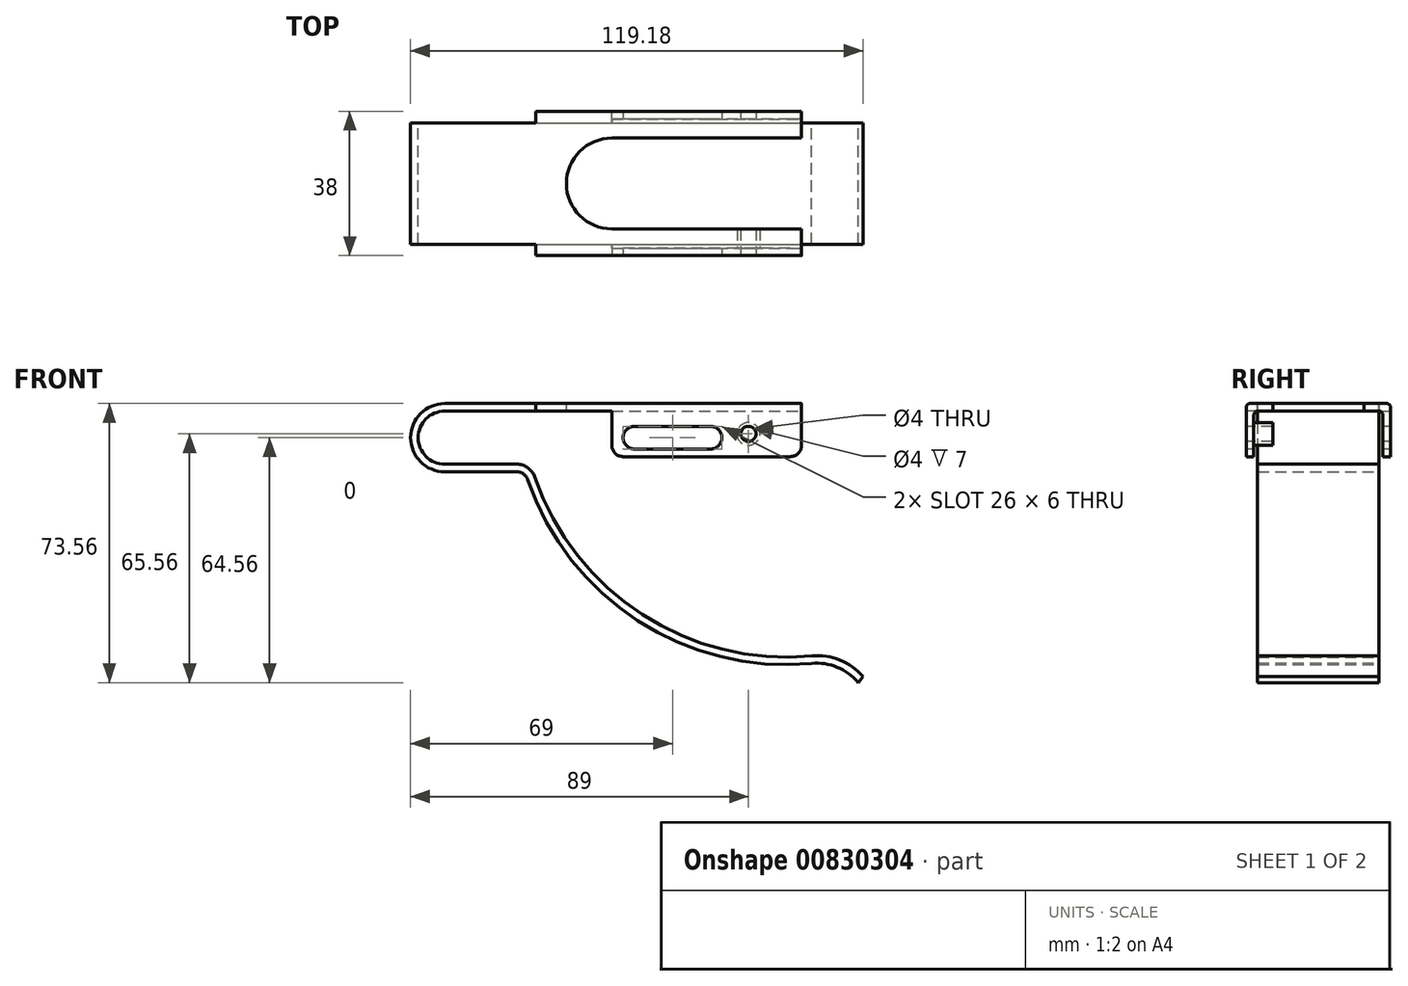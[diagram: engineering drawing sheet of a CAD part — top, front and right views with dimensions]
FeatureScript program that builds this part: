
annotation { "Feature Type Name" : "Feature", "Feature Type Description" : "" }
export const myFeature = defineFeature(function(context is Context, id is Id, definition is map)
    precondition{}
    {
        {
            var Q0;
            Q0=qCreatedBy(makeId("Front.planeOp"),FACE);
            var sketch = newSketch(context, id + "F0", { "sketchPlane" : qUnion([Q0])});
            skArc(sketch, "E0", {"start": v(0, 9) * mm, "mid": v(-9, 0) * mm, "end": v(0, -9) * mm});
            skLineSegment(sketch, "E1", {"start": v(0, 9) * mm, "end": v(94, 9) * mm});
            skLineSegment(sketch, "E2", {"start": v(0, -9) * mm, "end": v(19, -9) * mm});
            skArc(sketch, "E3", {"start": v(21.84, -11.03) * mm, "mid": v(50.83, -48.25) * mm, "end": v(96.64, -59.53) * mm});
            skArc(sketch, "E4", {"start": v(108.88, -64.56) * mm, "mid": v(103.39, -60.5) * mm, "end": v(96.64, -59.53) * mm});
            skPoint(sketch, "E5.visualSharp", {"position": v(21.18, -9) * mm});
            skArc(sketch, "E5.filletArc", {"start": v(21.84, -11.03) * mm, "mid": v(20.75, -9.56) * mm, "end": v(19, -9) * mm});
            skLineSegment(sketch, "E6.0", {"start": v(0, 7) * mm, "end": v(94, 7) * mm});
            skArc(sketch, "E6.1", {"start": v(0, 7) * mm, "mid": v(-7, 0) * mm, "end": v(0, -7) * mm});
            skArc(sketch, "E6.2", {"start": v(110.18, -63) * mm, "mid": v(104.1, -58.63) * mm, "end": v(96.7, -57.51) * mm});
            skArc(sketch, "E6.3", {"start": v(23.73, -10.39) * mm, "mid": v(52.02, -46.64) * mm, "end": v(96.7, -57.51) * mm});
            skArc(sketch, "E6.4", {"start": v(23.73, -10.39) * mm, "mid": v(21.91, -7.93) * mm, "end": v(19, -7) * mm});
            skLineSegment(sketch, "E6.5", {"start": v(0, -7) * mm, "end": v(19, -7) * mm});
            skLineSegment(sketch, "E7", {"start": v(94, 9) * mm, "end": v(94, 7) * mm});
            skLineSegment(sketch, "E8", {"start": v(110.18, -63) * mm, "end": v(108.88, -64.56) * mm});
            skSolve(sketch);
        }
        {
            var Q0;
            Q0=qSketchRegion(id+"F0",true);
            extrude(context, id + "F1", {"entities" : qUnion([Q0]), "depth" : 16 * mm, "offsetDistance" : 25 * mm});
        }
        {
            var Q0;
            Q0=makeQuery(id+"F1.opExtrude","SWEPT_FACE",FACE,{"disambiguationData":[OSD([sQuery(id+"F0.wireOp",EDGE,"E1")])]});
            var sketch = newSketch(context, id + "F2", { "sketchPlane" : qUnion([Q0])});
            skLineSegment(sketch, "E9.bottom", {"start": v(94, -16) * mm, "end": v(24, -16) * mm});
            skLineSegment(sketch, "E9.top", {"start": v(94, -19) * mm, "end": v(24, -19) * mm});
            skLineSegment(sketch, "E9.left", {"start": v(94, -16) * mm, "end": v(94, -19) * mm});
            skLineSegment(sketch, "E9.right", {"start": v(24, -16) * mm, "end": v(24, -19) * mm});
            skSolve(sketch);
        }
        {
            var Q0;
            Q0=qSketchRegion(id+"F2",true);
            extrude(context, id + "F3", {"entities" : qUnion([Q0]), "operationType" : NewBodyOperationType.ADD, "oppositeDirection" : true, "depth" : 2 * mm, "offsetDistance" : 25 * mm});
        }
        {
            var Q0;
            Q0=makeQuery(id+"F3.opExtrude","SWEPT_FACE",FACE,{"disambiguationData":[OSD([sQuery(id+"F2.wireOp",EDGE,"E9.top")])]});
            var sketch = newSketch(context, id + "F4", { "sketchPlane" : qUnion([Q0])});
            skLineSegment(sketch, "E10.bottom", {"start": v(94, 9) * mm, "end": v(44, 9) * mm});
            skLineSegment(sketch, "E10.top", {"start": v(94, -5) * mm, "end": v(44, -5) * mm});
            skLineSegment(sketch, "E10.left", {"start": v(94, 9) * mm, "end": v(94, -5) * mm});
            skLineSegment(sketch, "E10.right", {"start": v(44, 9) * mm, "end": v(44, -5) * mm});
            skSolve(sketch);
        }
        {
            var Q0;
            Q0=qSketchRegion(id+"F4",true);
            extrude(context, id + "F5", {"entities" : qUnion([Q0]), "operationType" : NewBodyOperationType.ADD, "oppositeDirection" : true, "depth" : 2 * mm, "offsetDistance" : 25 * mm});
        }
        {
            var Q0;
            Q0=makeQuery(id+"F3.opExtrude","CAP_EDGE",EDGE,{"disambiguationData":[OSD([sQuery(id+"F2.wireOp",EDGE,"E9.top")])],"isStart":true});
            var Q1;
            Q1=makeQuery(id+"F5.boolean.opBoolean","INTERSECT",EDGE,{"derivedFrom":[makeQuery(id+"F3.boolean.opBoolean","MERGE",FACE,{"derivedFrom":[makeQuery(id+"F1.opExtrude","SWEPT_FACE",FACE,{"disambiguationData":[OSD([sQuery(id+"F0.wireOp",EDGE,"E6.0")])]}),makeQuery(id+"F3.opExtrude","CAP_FACE",FACE,{"disambiguationData":[OSD([sQuery(id+"F2.wireOp",EDGE,"E9.bottom"),sQuery(id+"F2.wireOp",EDGE,"E9.top"),sQuery(id+"F2.wireOp",EDGE,"E9.left"),sQuery(id+"F2.wireOp",EDGE,"E9.right")])],"isStart":false})]}),makeQuery(id+"F5.opExtrude","CAP_FACE",FACE,{"disambiguationData":[OSD([sQuery(id+"F4.wireOp",EDGE,"E10.bottom"),sQuery(id+"F4.wireOp",EDGE,"E10.top"),sQuery(id+"F4.wireOp",EDGE,"E10.left"),sQuery(id+"F4.wireOp",EDGE,"E10.right")])],"isStart":false})]});
            fillet(context, id + "F6", {"entities" : qUnion([Q0, Q1]), "radius" : 1 * mm, "allowEdgeOverflow" : false});
        }
        {
            var Q0;
            Q0=makeQuery(id+"F1.opExtrude","SWEPT_BODY",BODY,{"disambiguationData":[OSD([sQuery(id+"F0.wireOp",EDGE,"E0"),sQuery(id+"F0.wireOp",EDGE,"E1"),sQuery(id+"F0.wireOp",EDGE,"E2"),sQuery(id+"F0.wireOp",EDGE,"E3"),sQuery(id+"F0.wireOp",EDGE,"E4"),sQuery(id+"F0.wireOp",EDGE,"E5.filletArc"),sQuery(id+"F0.wireOp",EDGE,"E6.0"),sQuery(id+"F0.wireOp",EDGE,"E6.1"),sQuery(id+"F0.wireOp",EDGE,"E6.2"),sQuery(id+"F0.wireOp",EDGE,"E6.3"),sQuery(id+"F0.wireOp",EDGE,"E6.4"),sQuery(id+"F0.wireOp",EDGE,"E6.5"),sQuery(id+"F0.wireOp",EDGE,"E7"),sQuery(id+"F0.wireOp",EDGE,"E8")])]});
            var Q1;
            Q1=qCreatedBy(makeId("Front.planeOp"),FACE);
            mirror(context, id + "F7", {"operationType" : NewBodyOperationType.ADD, "entities" : qUnion([Q0]), "mirrorPlane" : qUnion([Q1])});
        }
        {
            var Q0;
            {var subQ0=makeQuery(id+"F3.boolean.opBoolean","MERGE",FACE,{"derivedFrom":[makeQuery(id+"F1.opExtrude","SWEPT_FACE",FACE,{"disambiguationData":[OSD([sQuery(id+"F0.wireOp",EDGE,"E1")])]}),makeQuery(id+"F3.opExtrude","CAP_FACE",FACE,{"disambiguationData":[OSD([sQuery(id+"F2.wireOp",EDGE,"E9.bottom"),sQuery(id+"F2.wireOp",EDGE,"E9.top"),sQuery(id+"F2.wireOp",EDGE,"E9.left"),sQuery(id+"F2.wireOp",EDGE,"E9.right")])],"isStart":true})]});Q0=makeQuery(id+"F7.boolean.opBoolean","MERGE",FACE,{"derivedFrom":[subQ0,makeQuery(id+"F7.opPattern","COPY",FACE,{"derivedFrom":subQ0,"instanceName":"1"})]});}
            var sketch = newSketch(context, id + "F8", { "sketchPlane" : qUnion([Q0])});
            skArc(sketch, "E11", {"start": v(44, 11.96) * mm, "mid": v(32.04, 0) * mm, "end": v(44, -11.96) * mm});
            skLineSegment(sketch, "E12", {"start": v(44, 11.96) * mm, "end": v(94, 11.96) * mm});
            skLineSegment(sketch, "E13", {"start": v(44, -11.96) * mm, "end": v(94, -11.96) * mm});
            skLineSegment(sketch, "E14", {"start": v(94, 11.96) * mm, "end": v(94, -11.96) * mm});
            skSolve(sketch);
        }
        {
            var Q0;
            Q0=qSketchRegion(id+"F8",true);
            extrude(context, id + "F9", {"entities" : qUnion([Q0]), "operationType" : NewBodyOperationType.REMOVE, "oppositeDirection" : true, "depth" : 2 * mm, "offsetDistance" : 25 * mm});
        }
        {
            var Q0;
            Q0=makeQuery(id+"F5.boolean.opBoolean","MERGE",FACE,{"derivedFrom":[makeQuery(id+"F3.opExtrude","SWEPT_FACE",FACE,{"disambiguationData":[OSD([sQuery(id+"F2.wireOp",EDGE,"E9.top")])]}),makeQuery(id+"F5.opExtrude","CAP_FACE",FACE,{"disambiguationData":[OSD([sQuery(id+"F4.wireOp",EDGE,"E10.bottom"),sQuery(id+"F4.wireOp",EDGE,"E10.top"),sQuery(id+"F4.wireOp",EDGE,"E10.left"),sQuery(id+"F4.wireOp",EDGE,"E10.right")])],"isStart":true})]});
            var sketch = newSketch(context, id + "F10", { "sketchPlane" : qUnion([Q0])});
            skLineSegment(sketch, "E15", {"start": v(50, 0) * mm, "end": v(70, 0) * mm});
            skArc(sketch, "E16.0.startCap", {"start": v(50, -3) * mm, "mid": v(47, 0) * mm, "end": v(50, 3) * mm});
            skArc(sketch, "E16.0.endCap", {"start": v(70, 3) * mm, "mid": v(73, 0) * mm, "end": v(70, -3) * mm});
            skLineSegment(sketch, "E16.0.left", {"start": v(50, 3) * mm, "end": v(70, 3) * mm});
            skLineSegment(sketch, "E16.0.right", {"start": v(50, -3) * mm, "end": v(70, -3) * mm});
            skSolve(sketch);
        }
        {
            var Q0;
            Q0=qSketchRegion(id+"F10",true);
            extrude(context, id + "F11", {"entities" : qUnion([Q0]), "operationType" : NewBodyOperationType.REMOVE, "endBound" : BoundingType.THROUGH_ALL, "oppositeDirection" : true, "depth" : 25 * mm, "offsetDistance" : 25 * mm});
        }
        {
            var Q0;
            Q0=makeQuery(id+"F5.boolean.opBoolean","MERGE",FACE,{"derivedFrom":[makeQuery(id+"F3.opExtrude","SWEPT_FACE",FACE,{"disambiguationData":[OSD([sQuery(id+"F2.wireOp",EDGE,"E9.top")])]}),makeQuery(id+"F5.opExtrude","CAP_FACE",FACE,{"disambiguationData":[OSD([sQuery(id+"F4.wireOp",EDGE,"E10.bottom"),sQuery(id+"F4.wireOp",EDGE,"E10.top"),sQuery(id+"F4.wireOp",EDGE,"E10.left"),sQuery(id+"F4.wireOp",EDGE,"E10.right")])],"isStart":true})]});
            var sketch = newSketch(context, id + "F12", { "sketchPlane" : qUnion([Q0])});
            skPoint(sketch, "E17", {"position": v(80, 1) * mm});
            skSolve(sketch);
        }
        {
            var Q0;
            Q0=sQuery(id+"F12.wireOp",VERTEX,"E17");
            var Q1;
            Q1=makeQuery(id+"F1.opExtrude","SWEPT_BODY",BODY,{"disambiguationData":[OSD([sQuery(id+"F0.wireOp",EDGE,"E0"),sQuery(id+"F0.wireOp",EDGE,"E1"),sQuery(id+"F0.wireOp",EDGE,"E2"),sQuery(id+"F0.wireOp",EDGE,"E3"),sQuery(id+"F0.wireOp",EDGE,"E4"),sQuery(id+"F0.wireOp",EDGE,"E5.filletArc"),sQuery(id+"F0.wireOp",EDGE,"E6.0"),sQuery(id+"F0.wireOp",EDGE,"E6.1"),sQuery(id+"F0.wireOp",EDGE,"E6.2"),sQuery(id+"F0.wireOp",EDGE,"E6.3"),sQuery(id+"F0.wireOp",EDGE,"E6.4"),sQuery(id+"F0.wireOp",EDGE,"E6.5"),sQuery(id+"F0.wireOp",EDGE,"E7"),sQuery(id+"F0.wireOp",EDGE,"E8")])]});
            hole(context, id + "F13", {"style" : HoleStyle.SIMPLE, "endStyle" : HoleEndStyle.THROUGH, "holeDiameter" : 4 * mm, "majorDiameter" : 5 * mm, "isTappedThrough" : true, "tappedDepth" : 12 * mm, "tapClearance" : 3, "locations" : qUnion([Q0]), "scope" : qUnion([Q1])});
        }
        {
            var Q0;
            Q0=makeQuery(id+"F5.opExtrude","CAP_FACE",FACE,{"disambiguationData":[OSD([sQuery(id+"F4.wireOp",EDGE,"E10.bottom"),sQuery(id+"F4.wireOp",EDGE,"E10.top"),sQuery(id+"F4.wireOp",EDGE,"E10.left"),sQuery(id+"F4.wireOp",EDGE,"E10.right")])],"isStart":false});
            var sketch = newSketch(context, id + "F14", { "sketchPlane" : qUnion([Q0])});
            skCircle(sketch, "E18.0", {"center": v(-80, 1) * mm, "radius": 3 * mm});
            skSolve(sketch);
        }
        {
            var Q0;
            Q0=makeQuery(id+"F14.imprint","IMPRINT",FACE,{"disambiguationData":[TD([[makeQuery(id+"F14.imprint","IMPRINT",EDGE,{"derivedFrom":sQuery(id+"F14.wireOp",EDGE,"E18.0")}),1.0]])]});
            extrude(context, id + "F15", {"entities" : qUnion([Q0]), "operationType" : NewBodyOperationType.ADD, "depth" : 5 * mm, "offsetDistance" : 25 * mm});
        }
        {
            var Q0;
            Q0=makeQuery(id+"F7.opPattern","COPY",EDGE,{"derivedFrom":makeQuery(id+"F5.opExtrude","SWEPT_EDGE",EDGE,{"disambiguationData":[OSD([sQuery(id+"F4.wireOp",EDGE,"E10.top"),sQuery(id+"F4.wireOp",EDGE,"E10.left")])]}),"instanceName":"1"});
            var Q1;
            Q1=makeQuery(id+"F5.opExtrude","SWEPT_EDGE",EDGE,{"disambiguationData":[OSD([sQuery(id+"F4.wireOp",EDGE,"E10.top"),sQuery(id+"F4.wireOp",EDGE,"E10.left")])]});
            var Q2;
            Q2=makeQuery(id+"F5.opExtrude","SWEPT_EDGE",EDGE,{"disambiguationData":[OSD([sQuery(id+"F4.wireOp",EDGE,"E10.top"),sQuery(id+"F4.wireOp",EDGE,"E10.right")])]});
            var Q3;
            Q3=makeQuery(id+"F7.opPattern","COPY",EDGE,{"derivedFrom":makeQuery(id+"F5.opExtrude","SWEPT_EDGE",EDGE,{"disambiguationData":[OSD([sQuery(id+"F4.wireOp",EDGE,"E10.top"),sQuery(id+"F4.wireOp",EDGE,"E10.right")])]}),"instanceName":"1"});
            fillet(context, id + "F16", {"entities" : qUnion([Q0, Q1, Q2, Q3]), "radius" : 3 * mm, "tangentPropagation" : true, "allowEdgeOverflow" : false});
        }
    });
